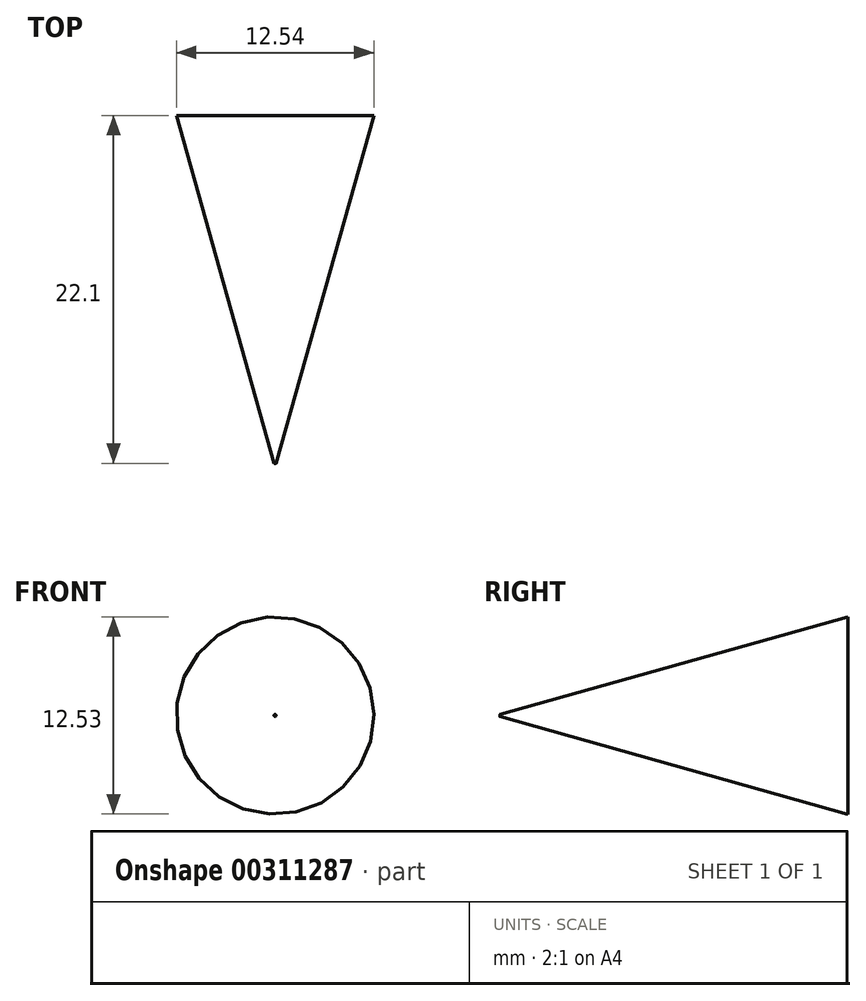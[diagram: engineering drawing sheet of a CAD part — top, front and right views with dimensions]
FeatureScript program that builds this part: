
annotation { "Feature Type Name" : "Feature", "Feature Type Description" : "" }
export const myFeature = defineFeature(function(context is Context, id is Id, definition is map)
    precondition{}
    {
        {
            var Q0;
            Q0=qCreatedBy(makeId("Front.planeOp"),FACE);
            var sketch = newSketch(context, id + "F0", { "sketchPlane" : qUnion([Q0])});
            skCircle(sketch, "E0", {"center": v(-33.88, 15.02) * mm, "radius": 6.27 * mm});
            skSolve(sketch);
        }
        {
            var Q0;
            Q0=qCreatedBy(makeId("Front.planeOp"),FACE);
            cPlane(context, id + "F1", {"entities" : qUnion([Q0]), "cplaneType" : CPlaneType.OFFSET, "offset" : 22.1 * mm, "width" : 152.4 * mm, "height" : 152.4 * mm});
        }
        {
            var Q0;
            Q0=qCreatedBy(id+"F1.planeOp",FACE);
            var sketch = newSketch(context, id + "F2", { "sketchPlane" : qUnion([Q0])});
            skCircle(sketch, "E1", {"center": v(-33.88, 15.02) * mm, "radius": 0.06 * mm});
            skSolve(sketch);
        }
        {
            var Q0;
            Q0=makeQuery(id+"F0.imprint","IMPRINT",FACE,{"disambiguationData":[TD([[makeQuery(id+"F0.imprint","IMPRINT",EDGE,{"derivedFrom":sQuery(id+"F0.wireOp",EDGE,"E0")}),1.0]])]});
            var Q1;
            Q1=makeQuery(id+"F2.imprint","IMPRINT",FACE,{"disambiguationData":[TD([[makeQuery(id+"F2.imprint","IMPRINT",EDGE,{"derivedFrom":sQuery(id+"F2.wireOp",EDGE,"E1")}),1.0]])]});
            loft(context, id + "F3", {"sheetProfilesArray" : [{ "sheetProfileEntities" : qUnion([Q0]) }, { "sheetProfileEntities" : qUnion([Q1]) }]});
        }
    });
